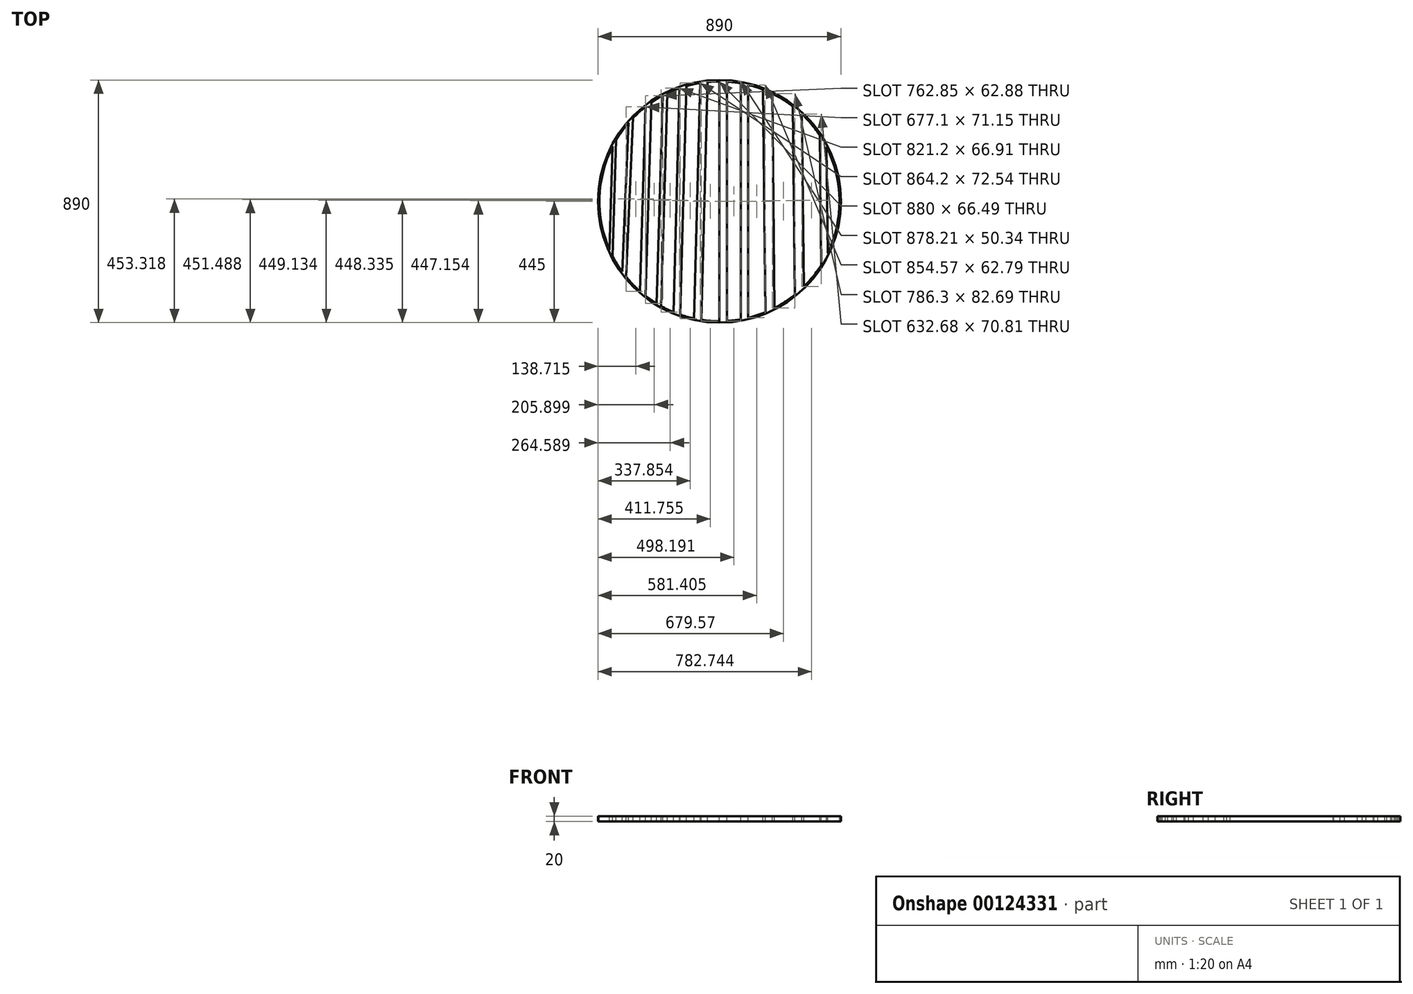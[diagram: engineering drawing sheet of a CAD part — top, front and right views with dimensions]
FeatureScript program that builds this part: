
annotation { "Feature Type Name" : "Feature", "Feature Type Description" : "" }
export const myFeature = defineFeature(function(context is Context, id is Id, definition is map)
    precondition{}
    {
        {
            var Q0;
            Q0=qCreatedBy(makeId("Top.planeOp"),FACE);
            var sketch = newSketch(context, id + "F0", { "sketchPlane" : qUnion([Q0])});
            skCircle(sketch, "E0", {"center": v(0, 0) * mm, "radius": 445 * mm});
            skCircle(sketch, "E1", {"center": v(0, 0) * mm, "radius": 440 * mm});
            skLineSegment(sketch, "E2", {"start": v(-391.2, 201.4) * mm, "end": v(-402.56, -177.6) * mm});
            skLineSegment(sketch, "E3", {"start": v(-378.81, 223.84) * mm, "end": v(-391.54, -200.74) * mm});
            skLineSegment(sketch, "E4", {"start": v(-332.7, 287.94) * mm, "end": v(-356.51, -257.87) * mm});
            skLineSegment(sketch, "E5", {"start": v(-316.44, 305.72) * mm, "end": v(-341.86, -277) * mm});
            skLineSegment(sketch, "E6", {"start": v(-249.52, 362.4) * mm, "end": v(-270.72, -353.18) * mm});
            skLineSegment(sketch, "E7", {"start": v(-270.7, 346.87) * mm, "end": v(-290.77, -330.23) * mm});
            skLineSegment(sketch, "E8", {"start": v(-207.66, 387.91) * mm, "end": v(-230.44, -380.69) * mm});
            skLineSegment(sketch, "E9", {"start": v(-190.72, 396.52) * mm, "end": v(-213.87, -384.53) * mm});
            skLineSegment(sketch, "E10", {"start": v(-146.96, 414.73) * mm, "end": v(-168.48, -406.47) * mm});
            skLineSegment(sketch, "E11", {"start": v(-121.43, 422.91) * mm, "end": v(-143.42, -415.97) * mm});
            skLineSegment(sketch, "E12", {"start": v(-70.74, 439.34) * mm, "end": v(-93.52, -429.95) * mm});
            skLineSegment(sketch, "E13", {"start": v(-43.62, 437.83) * mm, "end": v(-66.5, -434.95) * mm});
            skLineSegment(sketch, "E14", {"start": v(0, 440) * mm, "end": v(0, -445) * mm});
            skLineSegment(sketch, "E15", {"start": v(28.02, 439.1) * mm, "end": v(28.02, -439.1) * mm});
            skLineSegment(sketch, "E16", {"start": v(78.36, 432.97) * mm, "end": v(78.36, -432.97) * mm});
            skLineSegment(sketch, "E17", {"start": v(105.01, 427.29) * mm, "end": v(105.01, -427.29) * mm});
            skLineSegment(sketch, "E18", {"start": v(158.89, 410.31) * mm, "end": v(167.8, -406.75) * mm});
            skLineSegment(sketch, "E19", {"start": v(193.22, 395.3) * mm, "end": v(201.8, -391) * mm});
            skLineSegment(sketch, "E20", {"start": v(268.38, 348.67) * mm, "end": v(275.92, -342.74) * mm});
            skLineSegment(sketch, "E21", {"start": v(302.34, 319.67) * mm, "end": v(309.24, -313) * mm});
            skLineSegment(sketch, "E22", {"start": v(367.98, 241.23) * mm, "end": v(373.15, -233.15) * mm});
            skLineSegment(sketch, "E23", {"start": v(392.18, 199.5) * mm, "end": v(396.43, -190.9) * mm});
            skSolve(sketch);
        }
        {
            var Q0;
            {var subQ0=sQuery(id+"F0.wireOp",EDGE,"E6");var subQ1=sQuery(id+"F0.wireOp",EDGE,"E0");var subQ2=makeQuery(id+"F0.imprint","INTERSECT",VERTEX,{"derivedFrom":[subQ1,subQ0]});Q0=makeQuery(id+"F0.imprint","IMPRINT",FACE,{"disambiguationData":[TD([[makeQuery(id+"F0.imprint","IMPRINT",EDGE,{"disambiguationData":[TD([[subQ2,-1.0]])],"derivedFrom":subQ1}),1.0]])]});}
            var Q1;
            {var subQ0=sQuery(id+"F0.wireOp",EDGE,"E2");Q1=makeQuery(id+"F0.imprint","IMPRINT",FACE,{"disambiguationData":[TD([[makeQuery(id+"F0.imprint","IMPRINT",EDGE,{"derivedFrom":subQ0}),1.0]])]});}
            var Q2;
            {var subQ0=sQuery(id+"F0.wireOp",EDGE,"E4");Q2=makeQuery(id+"F0.imprint","IMPRINT",FACE,{"disambiguationData":[TD([[makeQuery(id+"F0.imprint","IMPRINT",EDGE,{"derivedFrom":subQ0}),1.0]])]});}
            var Q3;
            {var subQ3=sQuery(id+"F0.wireOp",EDGE,"E7");Q3=makeQuery(id+"F0.imprint","IMPRINT",FACE,{"disambiguationData":[TD([[makeQuery(id+"F0.imprint","IMPRINT",EDGE,{"derivedFrom":subQ3}),1.0]])]});}
            var Q4;
            {var subQ3=sQuery(id+"F0.wireOp",EDGE,"E9");Q4=makeQuery(id+"F0.imprint","IMPRINT",FACE,{"disambiguationData":[TD([[makeQuery(id+"F0.imprint","IMPRINT",EDGE,{"derivedFrom":subQ3}),-1.0]])]});}
            var Q5;
            {var subQ11=sQuery(id+"F0.wireOp",EDGE,"E6");var subQ12=sQuery(id+"F0.wireOp",EDGE,"E0");var subQ13=makeQuery(id+"F0.imprint","INTERSECT",VERTEX,{"derivedFrom":[subQ12,subQ11]});Q5=makeQuery(id+"F0.imprint","IMPRINT",FACE,{"disambiguationData":[TD([[makeQuery(id+"F0.imprint","IMPRINT",EDGE,{"disambiguationData":[TD([[subQ13,1.0]])],"derivedFrom":subQ12}),1.0]])]});}
            var Q6;
            {var subQ0=sQuery(id+"F0.wireOp",EDGE,"E10");Q6=makeQuery(id+"F0.imprint","IMPRINT",FACE,{"disambiguationData":[TD([[makeQuery(id+"F0.imprint","IMPRINT",EDGE,{"derivedFrom":subQ0}),1.0]])]});}
            var Q7;
            {var subQ0=sQuery(id+"F0.wireOp",EDGE,"E13");Q7=makeQuery(id+"F0.imprint","IMPRINT",FACE,{"disambiguationData":[TD([[makeQuery(id+"F0.imprint","IMPRINT",EDGE,{"derivedFrom":subQ0}),-1.0]])]});}
            var Q8;
            {var subQ3=sQuery(id+"F0.wireOp",EDGE,"E15");Q8=makeQuery(id+"F0.imprint","IMPRINT",FACE,{"disambiguationData":[TD([[makeQuery(id+"F0.imprint","IMPRINT",EDGE,{"derivedFrom":subQ3}),-1.0]])]});}
            var Q9;
            {var subQ0=sQuery(id+"F0.wireOp",EDGE,"E16");Q9=makeQuery(id+"F0.imprint","IMPRINT",FACE,{"disambiguationData":[TD([[makeQuery(id+"F0.imprint","IMPRINT",EDGE,{"derivedFrom":subQ0}),1.0]])]});}
            var Q10;
            {var subQ0=sQuery(id+"F0.wireOp",EDGE,"E18");Q10=makeQuery(id+"F0.imprint","IMPRINT",FACE,{"disambiguationData":[TD([[makeQuery(id+"F0.imprint","IMPRINT",EDGE,{"derivedFrom":subQ0}),1.0]])]});}
            var Q11;
            {var subQ0=sQuery(id+"F0.wireOp",EDGE,"E20");Q11=makeQuery(id+"F0.imprint","IMPRINT",FACE,{"disambiguationData":[TD([[makeQuery(id+"F0.imprint","IMPRINT",EDGE,{"derivedFrom":subQ0}),1.0]])]});}
            var Q12;
            {var subQ0=sQuery(id+"F0.wireOp",EDGE,"E22");Q12=makeQuery(id+"F0.imprint","IMPRINT",FACE,{"disambiguationData":[TD([[makeQuery(id+"F0.imprint","IMPRINT",EDGE,{"derivedFrom":subQ0}),1.0]])]});}
            var Q13;
            {var subQ15=sQuery(id+"F0.wireOp",EDGE,"E12");var subQ30=sQuery(id+"F0.wireOp",EDGE,"E0");var subQ31=makeQuery(id+"F0.imprint","INTERSECT",VERTEX,{"derivedFrom":[subQ30,subQ15]});Q13=makeQuery(id+"F0.imprint","IMPRINT",FACE,{"disambiguationData":[TD([[makeQuery(id+"F0.imprint","IMPRINT",EDGE,{"disambiguationData":[TD([[subQ31,1.0]])],"derivedFrom":subQ30}),1.0]])]});}
            var Q14;
            {var subQ4=sQuery(id+"F0.wireOp",EDGE,"E8");var subQ5=sQuery(id+"F0.wireOp",EDGE,"E0");var subQ6=makeQuery(id+"F0.imprint","INTERSECT",VERTEX,{"derivedFrom":[subQ5,subQ4]});Q14=makeQuery(id+"F0.imprint","IMPRINT",FACE,{"disambiguationData":[TD([[makeQuery(id+"F0.imprint","IMPRINT",EDGE,{"disambiguationData":[TD([[subQ6,-1.0]])],"derivedFrom":subQ5}),1.0]])]});}
            extrude(context, id + "F1", {"entities" : qUnion([Q0, Q1, Q2, Q3, Q4, Q5, Q6, Q7, Q8, Q9, Q10, Q11, Q12, Q13, Q14]), "oppositeDirection" : true, "depth" : 20 * mm});
        }
    });
